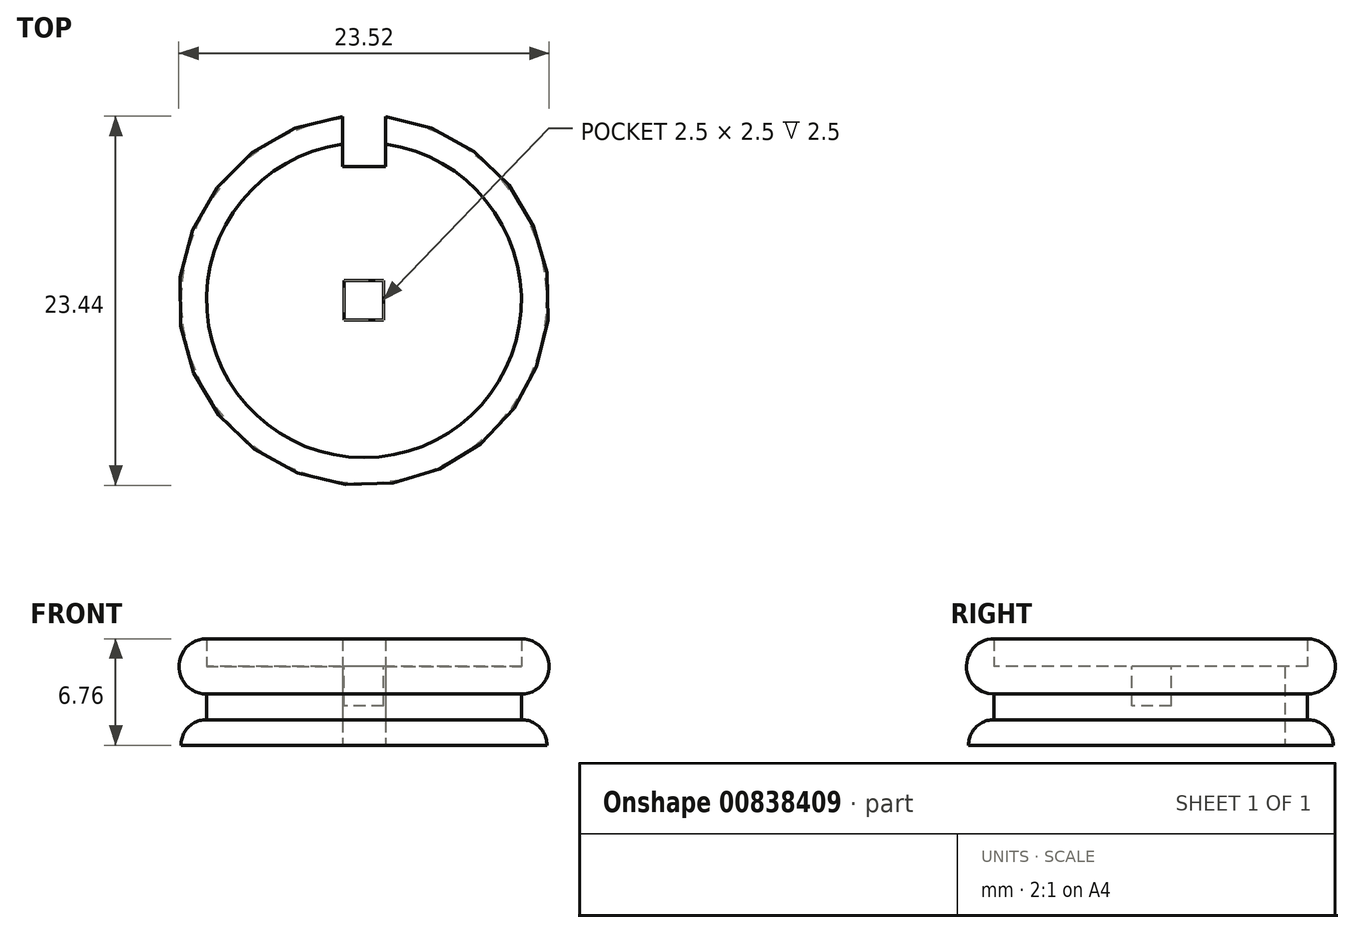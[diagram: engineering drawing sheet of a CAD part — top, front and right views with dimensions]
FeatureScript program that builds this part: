
annotation { "Feature Type Name" : "Feature", "Feature Type Description" : "" }
export const myFeature = defineFeature(function(context is Context, id is Id, definition is map)
    precondition{}
    {
        {
            var Q0;
            Q0=qCreatedBy(makeId("Front.planeOp"),FACE);
            var sketch = newSketch(context, id + "F0", { "sketchPlane" : qUnion([Q0])});
            skLineSegment(sketch, "E0", {"start": v(0, 0) * mm, "end": v(0, 5) * mm});
            skLineSegment(sketch, "E1", {"start": v(0, 0) * mm, "end": v(3.37, 0) * mm});
            skLineSegment(sketch, "E2", {"start": v(3.37, 0) * mm, "end": v(10, 0) * mm});
            skLineSegment(sketch, "E3", {"start": v(0, 5) * mm, "end": v(10, 5) * mm});
            skArc(sketch, "E4", {"start": v(11.62, 0) * mm, "mid": v(11.15, 1.15) * mm, "end": v(10, 1.62) * mm});
            skArc(sketch, "E5", {"start": v(10, 3.24) * mm, "mid": v(11.76, 5) * mm, "end": v(10, 6.76) * mm});
            skLineSegment(sketch, "E6", {"start": v(10, 3.24) * mm, "end": v(10, 1.62) * mm});
            skLineSegment(sketch, "E7", {"start": v(10, 0) * mm, "end": v(11.62, 0) * mm});
            skLineSegment(sketch, "E8", {"start": v(10, 5) * mm, "end": v(10, 6.76) * mm});
            skSolve(sketch);
        }
        {
            var Q0;
            Q0=makeQuery(id+"F0.imprint","IMPRINT",FACE,{"disambiguationData":[TD([[makeQuery(id+"F0.imprint","IMPRINT",EDGE,{"derivedFrom":sQuery(id+"F0.wireOp",EDGE,"E0")}),-1.0]])]});
            var Q1;
            Q1=sQuery(id+"F0.wireOp",EDGE,"E0");
            revolve(context, id + "F1", {"surfaceOperationType" : NewSurfaceOperationType.NEW, "entities" : qUnion([Q0]), "axis" : qUnion([Q1]), "revolveType" : RevolveType.FULL});
        }
        {
            var Q0;
            Q0=qCreatedBy(makeId("Top.planeOp"),FACE);
            var sketch = newSketch(context, id + "F2", { "sketchPlane" : qUnion([Q0])});
            skLineSegment(sketch, "E9.bottom", {"start": v(1.37, 13.47) * mm, "end": v(-1.37, 13.47) * mm});
            skLineSegment(sketch, "E9.top", {"start": v(1.37, 8.48) * mm, "end": v(-1.37, 8.48) * mm});
            skLineSegment(sketch, "E9.left", {"start": v(1.37, 13.47) * mm, "end": v(1.37, 8.48) * mm});
            skLineSegment(sketch, "E9.right", {"start": v(-1.37, 13.47) * mm, "end": v(-1.37, 8.48) * mm});
            skPoint(sketch, "E9.middle", {"position": v(0, 10.97) * mm});
            skSolve(sketch);
        }
        {
            var Q0;
            Q0=makeQuery(id+"F2.imprint","IMPRINT",FACE,{"disambiguationData":[TD([[makeQuery(id+"F2.imprint","IMPRINT",EDGE,{"derivedFrom":sQuery(id+"F2.wireOp",EDGE,"E9.bottom")}),1.0]])]});
            extrude(context, id + "F3", {"entities" : qUnion([Q0]), "operationType" : NewBodyOperationType.REMOVE, "depth" : 25 * mm, "offsetDistance" : 25 * mm});
        }
        {
            var Q0;
            Q0=makeQuery(id+"F1.opRevolve","SWEPT_FACE",FACE,{"disambiguationData":[OSD([sQuery(id+"F0.wireOp",EDGE,"E3")])]});
            var sketch = newSketch(context, id + "F4", { "sketchPlane" : qUnion([Q0])});
            skLineSegment(sketch, "E10.bottom", {"start": v(1.25, 1.25) * mm, "end": v(-1.25, 1.25) * mm});
            skLineSegment(sketch, "E10.top", {"start": v(1.25, -1.25) * mm, "end": v(-1.25, -1.25) * mm});
            skLineSegment(sketch, "E10.left", {"start": v(1.25, 1.25) * mm, "end": v(1.25, -1.25) * mm});
            skLineSegment(sketch, "E10.right", {"start": v(-1.25, 1.25) * mm, "end": v(-1.25, -1.25) * mm});
            skPoint(sketch, "E10.middle", {"position": v(0, 0) * mm});
            skSolve(sketch);
        }
        {
            var Q0;
            Q0=makeQuery(id+"F4.imprint","IMPRINT",FACE,{"disambiguationData":[TD([[makeQuery(id+"F4.imprint","IMPRINT",EDGE,{"derivedFrom":sQuery(id+"F4.wireOp",EDGE,"E10.bottom")}),1.0]])]});
            extrude(context, id + "F5", {"entities" : qUnion([Q0]), "operationType" : NewBodyOperationType.REMOVE, "oppositeDirection" : true, "depth" : 2.5 * mm, "offsetDistance" : 25 * mm});
        }
    });
